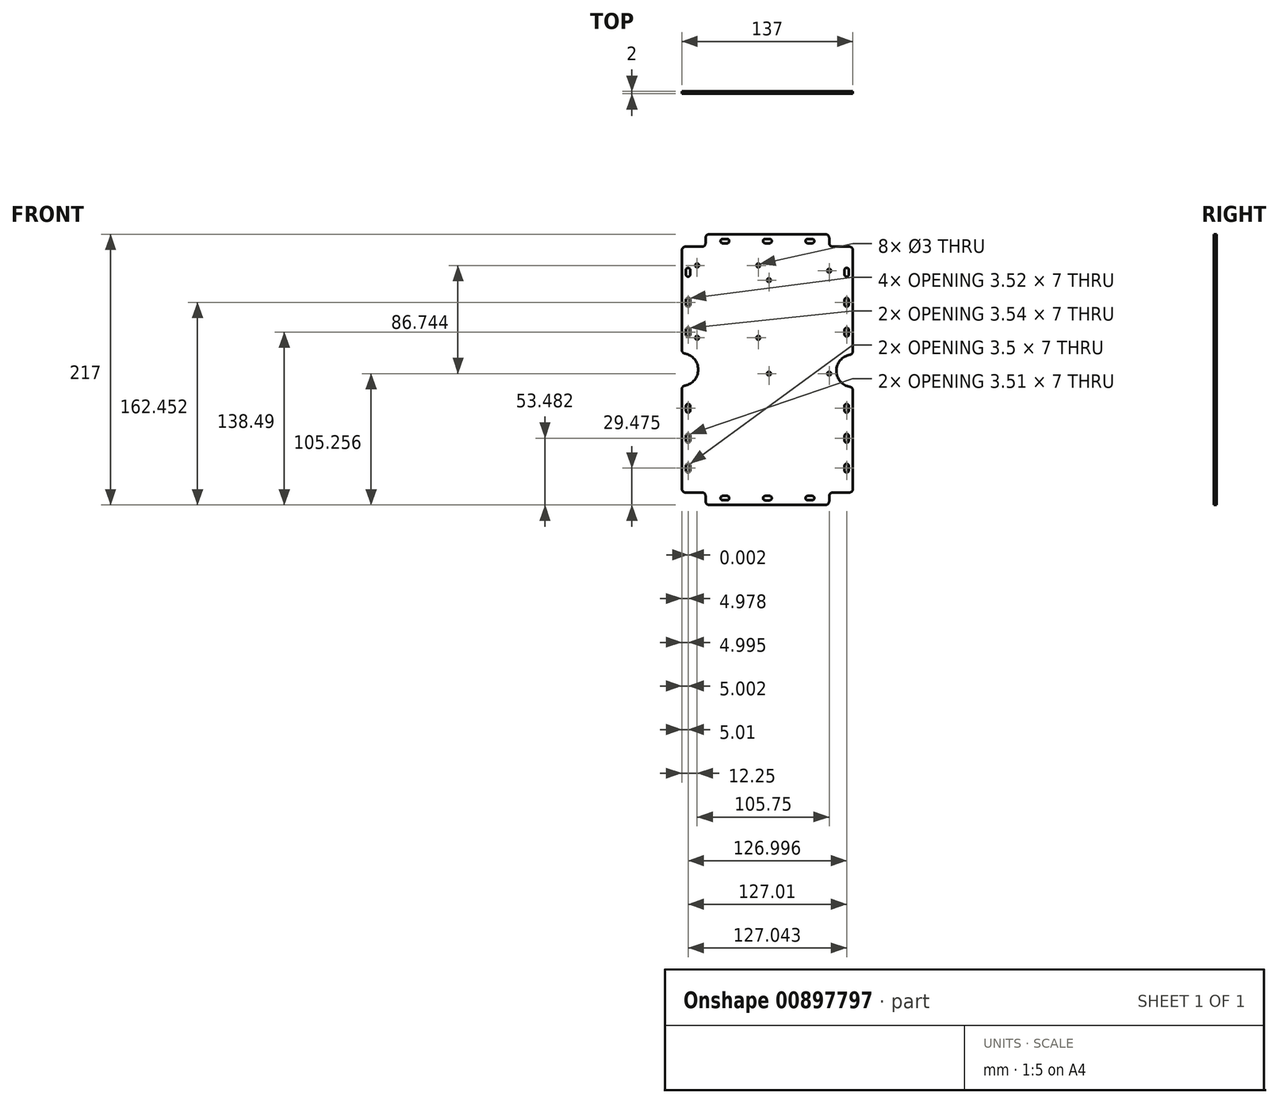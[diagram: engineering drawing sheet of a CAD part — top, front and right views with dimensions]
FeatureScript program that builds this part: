
annotation { "Feature Type Name" : "Feature", "Feature Type Description" : "" }
export const myFeature = defineFeature(function(context is Context, id is Id, definition is map)
    precondition{}
    {
        {
            var Q0;
            Q0=qCreatedBy(makeId("Front.planeOp"),FACE);
            var sketch = newSketch(context, id + "F0", { "sketchPlane" : qUnion([Q0])});
            skLineSegment(sketch, "E0", {"start": v(-49.5, 105.5) * mm, "end": v(-49.5, 101.5) * mm});
            skLineSegment(sketch, "E1", {"start": v(-52.5, 98.5) * mm, "end": v(-65.5, 98.5) * mm});
            skLineSegment(sketch, "E2", {"start": v(-68.5, 95.5) * mm, "end": v(-68.5, 15.73) * mm});
            skLineSegment(sketch, "E3.MirrorCS", {"start": v(-68.5, -95.5) * mm, "end": v(-68.5, -15.73) * mm});
            skLineSegment(sketch, "E4.MirrorCS", {"start": v(-52.5, -98.5) * mm, "end": v(-65.5, -98.5) * mm});
            skLineSegment(sketch, "E5.MirrorCS", {"start": v(-49.5, -105.5) * mm, "end": v(-49.5, -101.5) * mm});
            skLineSegment(sketch, "E6", {"start": v(-46.5, 108.5) * mm, "end": v(0, 108.5) * mm});
            skLineSegment(sketch, "E7.MirrorCS", {"start": v(-46.5, -108.5) * mm, "end": v(0, -108.5) * mm});
            skLineSegment(sketch, "E8.MirrorCS", {"start": v(46.5, 108.5) * mm, "end": v(0, 108.5) * mm});
            skLineSegment(sketch, "E9.MirrorCS", {"start": v(49.5, 105.5) * mm, "end": v(49.5, 101.5) * mm});
            skLineSegment(sketch, "E10.MirrorCS", {"start": v(68.5, 95.5) * mm, "end": v(68.5, 14.76) * mm});
            skLineSegment(sketch, "E11.MirrorCS", {"start": v(68.5, -95.5) * mm, "end": v(68.5, -16.73) * mm});
            skLineSegment(sketch, "E12.MirrorCS", {"start": v(52.5, -98.5) * mm, "end": v(65.5, -98.5) * mm});
            skLineSegment(sketch, "E13.MirrorCS", {"start": v(49.5, -105.5) * mm, "end": v(49.5, -101.5) * mm});
            skLineSegment(sketch, "E14.MirrorCS", {"start": v(46.5, -108.5) * mm, "end": v(0, -108.5) * mm});
            skPoint(sketch, "E15.visualSharp", {"position": v(-68.5, 98.5) * mm});
            skArc(sketch, "E15.filletArc", {"start": v(-65.5, 98.5) * mm, "mid": v(-67.62, 97.62) * mm, "end": v(-68.5, 95.5) * mm});
            skPoint(sketch, "E16.visualSharp", {"position": v(-49.5, 98.5) * mm});
            skArc(sketch, "E16.filletArc", {"start": v(-52.5, 98.5) * mm, "mid": v(-50.38, 99.38) * mm, "end": v(-49.5, 101.5) * mm});
            skPoint(sketch, "E17.visualSharp", {"position": v(-49.5, 108.5) * mm});
            skArc(sketch, "E17.filletArc", {"start": v(-46.5, 108.5) * mm, "mid": v(-48.62, 107.62) * mm, "end": v(-49.5, 105.5) * mm});
            skPoint(sketch, "E18.visualSharp", {"position": v(49.5, 108.5) * mm});
            skArc(sketch, "E18.filletArc", {"start": v(49.5, 105.5) * mm, "mid": v(48.62, 107.62) * mm, "end": v(46.5, 108.5) * mm});
            skPoint(sketch, "E19.visualSharp", {"position": v(49.5, 98.5) * mm});
            skArc(sketch, "E19.filletArc", {"start": v(49.5, 101.5) * mm, "mid": v(50.38, 99.38) * mm, "end": v(52.5, 98.5) * mm});
            skPoint(sketch, "E20.visualSharp", {"position": v(68.5, 98.5) * mm});
            skArc(sketch, "E20.filletArc", {"start": v(68.5, 95.5) * mm, "mid": v(67.62, 97.62) * mm, "end": v(65.5, 98.5) * mm});
            skPoint(sketch, "E21.visualSharp", {"position": v(-68.5, -98.5) * mm});
            skArc(sketch, "E21.filletArc", {"start": v(-68.5, -95.5) * mm, "mid": v(-67.62, -97.62) * mm, "end": v(-65.5, -98.5) * mm});
            skPoint(sketch, "E22.visualSharp", {"position": v(-49.5, -98.5) * mm});
            skArc(sketch, "E22.filletArc", {"start": v(-49.5, -101.5) * mm, "mid": v(-50.38, -99.38) * mm, "end": v(-52.5, -98.5) * mm});
            skPoint(sketch, "E23.visualSharp", {"position": v(-49.5, -108.5) * mm});
            skArc(sketch, "E23.filletArc", {"start": v(-49.5, -105.5) * mm, "mid": v(-48.62, -107.62) * mm, "end": v(-46.5, -108.5) * mm});
            skPoint(sketch, "E24.visualSharp", {"position": v(49.5, -108.5) * mm});
            skArc(sketch, "E24.filletArc", {"start": v(46.5, -108.5) * mm, "mid": v(48.62, -107.62) * mm, "end": v(49.5, -105.5) * mm});
            skPoint(sketch, "E25.visualSharp", {"position": v(68.5, -98.5) * mm});
            skArc(sketch, "E25.filletArc", {"start": v(65.5, -98.5) * mm, "mid": v(67.62, -97.62) * mm, "end": v(68.5, -95.5) * mm});
            skPoint(sketch, "E26.visualSharp", {"position": v(49.5, -98.5) * mm});
            skArc(sketch, "E26.filletArc", {"start": v(52.5, -98.5) * mm, "mid": v(50.38, -99.38) * mm, "end": v(49.5, -101.5) * mm});
            skCircle(sketch, "E27", {"center": v(0, 103) * mm, "radius": 1.75 * mm});
            skCircle(sketch, "E28", {"center": v(-34, 103) * mm, "radius": 1.75 * mm});
            skCircle(sketch, "E29", {"center": v(34, 103) * mm, "radius": 1.75 * mm});
            skCircle(sketch, "E30.MirrorC", {"center": v(-34, -103) * mm, "radius": 1.75 * mm});
            skCircle(sketch, "E31.MirrorC", {"center": v(0, -103) * mm, "radius": 1.75 * mm});
            skCircle(sketch, "E32.MirrorC", {"center": v(34, -103) * mm, "radius": 1.75 * mm});
            skPoint(sketch, "E33.centerSnap0", {"position": v(-59, 98.5) * mm});
            skCircle(sketch, "E34", {"center": v(-63.5, 54) * mm, "radius": 1.75 * mm});
            skCircle(sketch, "E35", {"center": v(-63.5, 30) * mm, "radius": 1.75 * mm});
            skCircle(sketch, "E36", {"center": v(-63.5, 78) * mm, "radius": 1.75 * mm});
            skCircle(sketch, "E37.MirrorC", {"center": v(63.5, 78) * mm, "radius": 1.75 * mm});
            skCircle(sketch, "E38.MirrorC", {"center": v(63.5, 54) * mm, "radius": 1.75 * mm});
            skCircle(sketch, "E39.MirrorC", {"center": v(63.5, 30) * mm, "radius": 1.75 * mm});
            skCircle(sketch, "E40", {"center": v(-63.5, -31) * mm, "radius": 1.75 * mm});
            skCircle(sketch, "E41", {"center": v(-63.5, -55) * mm, "radius": 1.75 * mm});
            skCircle(sketch, "E42", {"center": v(-63.5, -79) * mm, "radius": 1.75 * mm});
            skCircle(sketch, "E43.MirrorC", {"center": v(63.5, -31) * mm, "radius": 1.75 * mm});
            skCircle(sketch, "E44.MirrorC", {"center": v(63.5, -55) * mm, "radius": 1.75 * mm});
            skCircle(sketch, "E45.MirrorC", {"center": v(63.5, -79) * mm, "radius": 1.75 * mm});
            skLineSegment(sketch, "E46", {"start": v(-35.75, 103) * mm, "end": v(-32.25, 103) * mm});
            skArc(sketch, "E47.0.startCap", {"start": v(-35.75, 101.25) * mm, "mid": v(-37.5, 103) * mm, "end": v(-35.75, 104.75) * mm});
            skArc(sketch, "E47.0.endCap", {"start": v(-32.25, 104.75) * mm, "mid": v(-30.5, 103) * mm, "end": v(-32.25, 101.25) * mm});
            skLineSegment(sketch, "E47.0.left", {"start": v(-35.75, 104.75) * mm, "end": v(-32.25, 104.75) * mm});
            skLineSegment(sketch, "E47.0.right", {"start": v(-35.75, 101.25) * mm, "end": v(-32.25, 101.25) * mm});
            skArc(sketch, "E48.0.startCap", {"start": v(-1.74, 101.27) * mm, "mid": v(-3.5, 103.02) * mm, "end": v(-1.74, 104.77) * mm});
            skArc(sketch, "E48.0.endCap", {"start": v(1.76, 104.77) * mm, "mid": v(3.5, 103.02) * mm, "end": v(1.76, 101.27) * mm});
            skLineSegment(sketch, "E48.0.left", {"start": v(-1.74, 104.77) * mm, "end": v(1.76, 104.77) * mm});
            skLineSegment(sketch, "E48.0.right", {"start": v(-1.74, 101.27) * mm, "end": v(1.76, 101.27) * mm});
            skArc(sketch, "E49.0.startCap", {"start": v(32.33, 101.25) * mm, "mid": v(30.58, 103) * mm, "end": v(32.33, 104.75) * mm});
            skArc(sketch, "E49.0.endCap", {"start": v(35.83, 104.75) * mm, "mid": v(37.58, 103) * mm, "end": v(35.83, 101.25) * mm});
            skLineSegment(sketch, "E49.0.left", {"start": v(32.33, 104.75) * mm, "end": v(35.83, 104.75) * mm});
            skLineSegment(sketch, "E49.0.right", {"start": v(32.33, 101.25) * mm, "end": v(35.83, 101.25) * mm});
            skArc(sketch, "E50.MirrorCS", {"start": v(-35.75, -101.25) * mm, "mid": v(-37.5, -103) * mm, "end": v(-35.75, -104.75) * mm});
            skLineSegment(sketch, "E51.MirrorCS", {"start": v(-35.75, -104.75) * mm, "end": v(-32.25, -104.75) * mm});
            skArc(sketch, "E52.MirrorCS", {"start": v(-32.25, -104.75) * mm, "mid": v(-30.5, -103) * mm, "end": v(-32.25, -101.25) * mm});
            skLineSegment(sketch, "E53.MirrorCS", {"start": v(-35.75, -101.25) * mm, "end": v(-32.25, -101.25) * mm});
            skArc(sketch, "E54.MirrorCS", {"start": v(1.76, -104.77) * mm, "mid": v(3.5, -103.02) * mm, "end": v(1.76, -101.27) * mm});
            skLineSegment(sketch, "E55.MirrorCS", {"start": v(-1.74, -101.27) * mm, "end": v(1.76, -101.27) * mm});
            skLineSegment(sketch, "E56.MirrorCS", {"start": v(-1.74, -104.77) * mm, "end": v(1.76, -104.77) * mm});
            skArc(sketch, "E57.MirrorCS", {"start": v(-1.74, -101.27) * mm, "mid": v(-3.5, -103.02) * mm, "end": v(-1.74, -104.77) * mm});
            skArc(sketch, "E58.MirrorCS", {"start": v(32.33, -101.25) * mm, "mid": v(30.58, -103) * mm, "end": v(32.33, -104.75) * mm});
            skArc(sketch, "E59.MirrorCS", {"start": v(35.83, -104.75) * mm, "mid": v(37.58, -103) * mm, "end": v(35.83, -101.25) * mm});
            skLineSegment(sketch, "E60.MirrorCS", {"start": v(32.33, -104.75) * mm, "end": v(35.83, -104.75) * mm});
            skLineSegment(sketch, "E61.MirrorCS", {"start": v(32.33, -101.25) * mm, "end": v(35.83, -101.25) * mm});
            skLineSegment(sketch, "E62", {"start": v(-63.53, 79.75) * mm, "end": v(-63.53, 76.25) * mm});
            skArc(sketch, "E63.0.startCap", {"start": v(-65.28, 79.75) * mm, "mid": v(-63.53, 81.5) * mm, "end": v(-61.78, 79.75) * mm});
            skArc(sketch, "E63.0.endCap", {"start": v(-61.78, 76.25) * mm, "mid": v(-63.53, 74.5) * mm, "end": v(-65.28, 76.25) * mm});
            skLineSegment(sketch, "E63.0.left", {"start": v(-61.78, 79.75) * mm, "end": v(-61.78, 76.25) * mm});
            skLineSegment(sketch, "E63.0.right", {"start": v(-65.28, 79.75) * mm, "end": v(-65.28, 76.25) * mm});
            skArc(sketch, "E64.0.startCap", {"start": v(-65.23, 55.7) * mm, "mid": v(-63.48, 57.45) * mm, "end": v(-61.73, 55.7) * mm});
            skArc(sketch, "E64.0.endCap", {"start": v(-61.73, 52.2) * mm, "mid": v(-63.48, 50.45) * mm, "end": v(-65.23, 52.2) * mm});
            skLineSegment(sketch, "E64.0.left", {"start": v(-61.73, 55.7) * mm, "end": v(-61.73, 52.2) * mm});
            skLineSegment(sketch, "E64.0.right", {"start": v(-65.23, 55.7) * mm, "end": v(-65.23, 52.2) * mm});
            skArc(sketch, "E65.0.startCap", {"start": v(-65.3, 31.74) * mm, "mid": v(-63.54, 33.5) * mm, "end": v(-61.8, 31.74) * mm});
            skArc(sketch, "E65.0.endCap", {"start": v(-61.8, 28.24) * mm, "mid": v(-63.54, 26.5) * mm, "end": v(-65.3, 28.24) * mm});
            skLineSegment(sketch, "E65.0.left", {"start": v(-61.8, 31.74) * mm, "end": v(-61.8, 28.24) * mm});
            skLineSegment(sketch, "E65.0.right", {"start": v(-65.3, 31.74) * mm, "end": v(-65.3, 28.24) * mm});
            skArc(sketch, "E66.MirrorCS", {"start": v(65.28, 79.75) * mm, "mid": v(63.53, 81.5) * mm, "end": v(61.78, 79.75) * mm});
            skLineSegment(sketch, "E67.MirrorCS", {"start": v(61.78, 79.75) * mm, "end": v(61.78, 76.25) * mm});
            skArc(sketch, "E68.MirrorCS", {"start": v(61.78, 76.25) * mm, "mid": v(63.53, 74.5) * mm, "end": v(65.28, 76.25) * mm});
            skLineSegment(sketch, "E69.MirrorCS", {"start": v(65.28, 79.75) * mm, "end": v(65.28, 76.25) * mm});
            skArc(sketch, "E70.MirrorCS", {"start": v(65.23, 55.7) * mm, "mid": v(63.48, 57.45) * mm, "end": v(61.73, 55.7) * mm});
            skLineSegment(sketch, "E71.MirrorCS", {"start": v(61.73, 55.7) * mm, "end": v(61.73, 52.2) * mm});
            skLineSegment(sketch, "E72.MirrorCS", {"start": v(65.23, 55.7) * mm, "end": v(65.23, 52.2) * mm});
            skArc(sketch, "E73.MirrorCS", {"start": v(61.73, 52.2) * mm, "mid": v(63.48, 50.45) * mm, "end": v(65.23, 52.2) * mm});
            skArc(sketch, "E74.MirrorCS", {"start": v(65.3, 31.74) * mm, "mid": v(63.54, 33.5) * mm, "end": v(61.8, 31.74) * mm});
            skLineSegment(sketch, "E75.MirrorCS", {"start": v(61.8, 31.74) * mm, "end": v(61.8, 28.24) * mm});
            skArc(sketch, "E76.MirrorCS", {"start": v(61.8, 28.24) * mm, "mid": v(63.54, 26.5) * mm, "end": v(65.3, 28.24) * mm});
            skLineSegment(sketch, "E77.MirrorCS", {"start": v(65.3, 31.74) * mm, "end": v(65.3, 28.24) * mm});
            skArc(sketch, "E78.0.startCap", {"start": v(-65.23, -29.25) * mm, "mid": v(-63.48, -27.5) * mm, "end": v(-61.73, -29.25) * mm});
            skArc(sketch, "E78.0.endCap", {"start": v(-61.73, -32.75) * mm, "mid": v(-63.48, -34.5) * mm, "end": v(-65.23, -32.75) * mm});
            skLineSegment(sketch, "E78.0.left", {"start": v(-61.73, -29.25) * mm, "end": v(-61.73, -32.75) * mm});
            skLineSegment(sketch, "E78.0.right", {"start": v(-65.23, -29.25) * mm, "end": v(-65.23, -32.75) * mm});
            skArc(sketch, "E79.0.startCap", {"start": v(-65.26, -53.27) * mm, "mid": v(-63.51, -51.52) * mm, "end": v(-61.76, -53.27) * mm});
            skArc(sketch, "E79.0.endCap", {"start": v(-61.76, -56.77) * mm, "mid": v(-63.51, -58.52) * mm, "end": v(-65.26, -56.77) * mm});
            skLineSegment(sketch, "E79.0.left", {"start": v(-61.76, -53.27) * mm, "end": v(-61.76, -56.77) * mm});
            skLineSegment(sketch, "E79.0.right", {"start": v(-65.26, -53.27) * mm, "end": v(-65.26, -56.77) * mm});
            skArc(sketch, "E80.0.startCap", {"start": v(-65.25, -77.28) * mm, "mid": v(-63.5, -75.53) * mm, "end": v(-61.75, -77.28) * mm});
            skArc(sketch, "E80.0.endCap", {"start": v(-61.75, -80.77) * mm, "mid": v(-63.5, -82.52) * mm, "end": v(-65.25, -80.77) * mm});
            skLineSegment(sketch, "E80.0.left", {"start": v(-61.75, -77.28) * mm, "end": v(-61.75, -80.77) * mm});
            skLineSegment(sketch, "E80.0.right", {"start": v(-65.25, -77.28) * mm, "end": v(-65.25, -80.77) * mm});
            skArc(sketch, "E81.MirrorCS", {"start": v(65.23, -29.25) * mm, "mid": v(63.48, -27.5) * mm, "end": v(61.73, -29.25) * mm});
            skLineSegment(sketch, "E82.MirrorCS", {"start": v(61.73, -29.25) * mm, "end": v(61.73, -32.75) * mm});
            skArc(sketch, "E83.MirrorCS", {"start": v(61.73, -32.75) * mm, "mid": v(63.48, -34.5) * mm, "end": v(65.23, -32.75) * mm});
            skLineSegment(sketch, "E84.MirrorCS", {"start": v(65.23, -29.25) * mm, "end": v(65.23, -32.75) * mm});
            skLineSegment(sketch, "E85.MirrorCS", {"start": v(61.76, -53.27) * mm, "end": v(61.76, -56.77) * mm});
            skArc(sketch, "E86.MirrorCS", {"start": v(65.26, -53.27) * mm, "mid": v(63.51, -51.52) * mm, "end": v(61.76, -53.27) * mm});
            skLineSegment(sketch, "E87.MirrorCS", {"start": v(65.26, -53.27) * mm, "end": v(65.26, -56.77) * mm});
            skArc(sketch, "E88.MirrorCS", {"start": v(61.76, -56.77) * mm, "mid": v(63.51, -58.52) * mm, "end": v(65.26, -56.77) * mm});
            skArc(sketch, "E89.MirrorCS", {"start": v(61.75, -80.77) * mm, "mid": v(63.5, -82.52) * mm, "end": v(65.25, -80.77) * mm});
            skArc(sketch, "E90.MirrorCS", {"start": v(65.25, -77.28) * mm, "mid": v(63.5, -75.53) * mm, "end": v(61.75, -77.28) * mm});
            skLineSegment(sketch, "E91.MirrorCS", {"start": v(65.25, -77.28) * mm, "end": v(65.25, -80.77) * mm});
            skLineSegment(sketch, "E92.MirrorCS", {"start": v(61.75, -77.28) * mm, "end": v(61.75, -80.77) * mm});
            skCircle(sketch, "E93", {"center": v(-56.25, 83.5) * mm, "radius": 1.5 * mm});
            skCircle(sketch, "E94", {"center": v(-56.25, 25.5) * mm, "radius": 1.5 * mm});
            skCircle(sketch, "E95", {"center": v(-7.25, 25.5) * mm, "radius": 1.5 * mm});
            skCircle(sketch, "E96", {"center": v(-7.25, 83.5) * mm, "radius": 1.5 * mm});
            skPoint(sketch, "E97.startSnap0", {"position": v(-68.42, 0) * mm});
            skArc(sketch, "E98", {"start": v(-66.05, 12.78) * mm, "mid": v(-55.42, 0) * mm, "end": v(-66.05, -12.78) * mm});
            skPoint(sketch, "E99.visualSharp", {"position": v(-68.5, 13) * mm});
            skArc(sketch, "E99.filletArc", {"start": v(-68.5, 15.73) * mm, "mid": v(-67.8, 13.81) * mm, "end": v(-66.05, 12.78) * mm});
            skPoint(sketch, "E100.visualSharp", {"position": v(-68.5, -13) * mm});
            skArc(sketch, "E100.filletArc", {"start": v(-66.05, -12.78) * mm, "mid": v(-67.8, -13.81) * mm, "end": v(-68.5, -15.73) * mm});
            skArc(sketch, "E101", {"start": v(66.03, 11.81) * mm, "mid": v(55.32, -0.98) * mm, "end": v(66.03, -13.78) * mm});
            skPoint(sketch, "E102.visualSharp", {"position": v(68.5, 12.01) * mm});
            skArc(sketch, "E102.filletArc", {"start": v(66.03, 11.81) * mm, "mid": v(67.8, 12.84) * mm, "end": v(68.5, 14.76) * mm});
            skPoint(sketch, "E103.visualSharp", {"position": v(68.5, -13.98) * mm});
            skArc(sketch, "E103.filletArc", {"start": v(68.5, -16.73) * mm, "mid": v(67.8, -14.8) * mm, "end": v(66.03, -13.78) * mm});
            skCircle(sketch, "E104", {"center": v(1.25, 71.66) * mm, "radius": 1.5 * mm});
            skCircle(sketch, "E105", {"center": v(1.25, -3.24) * mm, "radius": 1.5 * mm});
            skCircle(sketch, "E106", {"center": v(49.5, 79.26) * mm, "radius": 1.5 * mm});
            skCircle(sketch, "E107", {"center": v(49.5, -3.24) * mm, "radius": 1.5 * mm});
            skLineSegment(sketch, "E108", {"start": v(52.5, 98.5) * mm, "end": v(65.5, 98.5) * mm});
            skSolve(sketch);
        }
        {
            var Q0;
            Q0=makeQuery(id+"F0.imprint","IMPRINT",FACE,{"disambiguationData":[TD([[makeQuery(id+"F0.imprint","IMPRINT",EDGE,{"derivedFrom":sQuery(id+"F0.wireOp",EDGE,"E0")}),1.0]])]});
            extrude(context, id + "F1", {"entities" : qUnion([Q0]), "depth" : 2 * mm, "offsetDistance" : 25 * mm});
        }
    });
